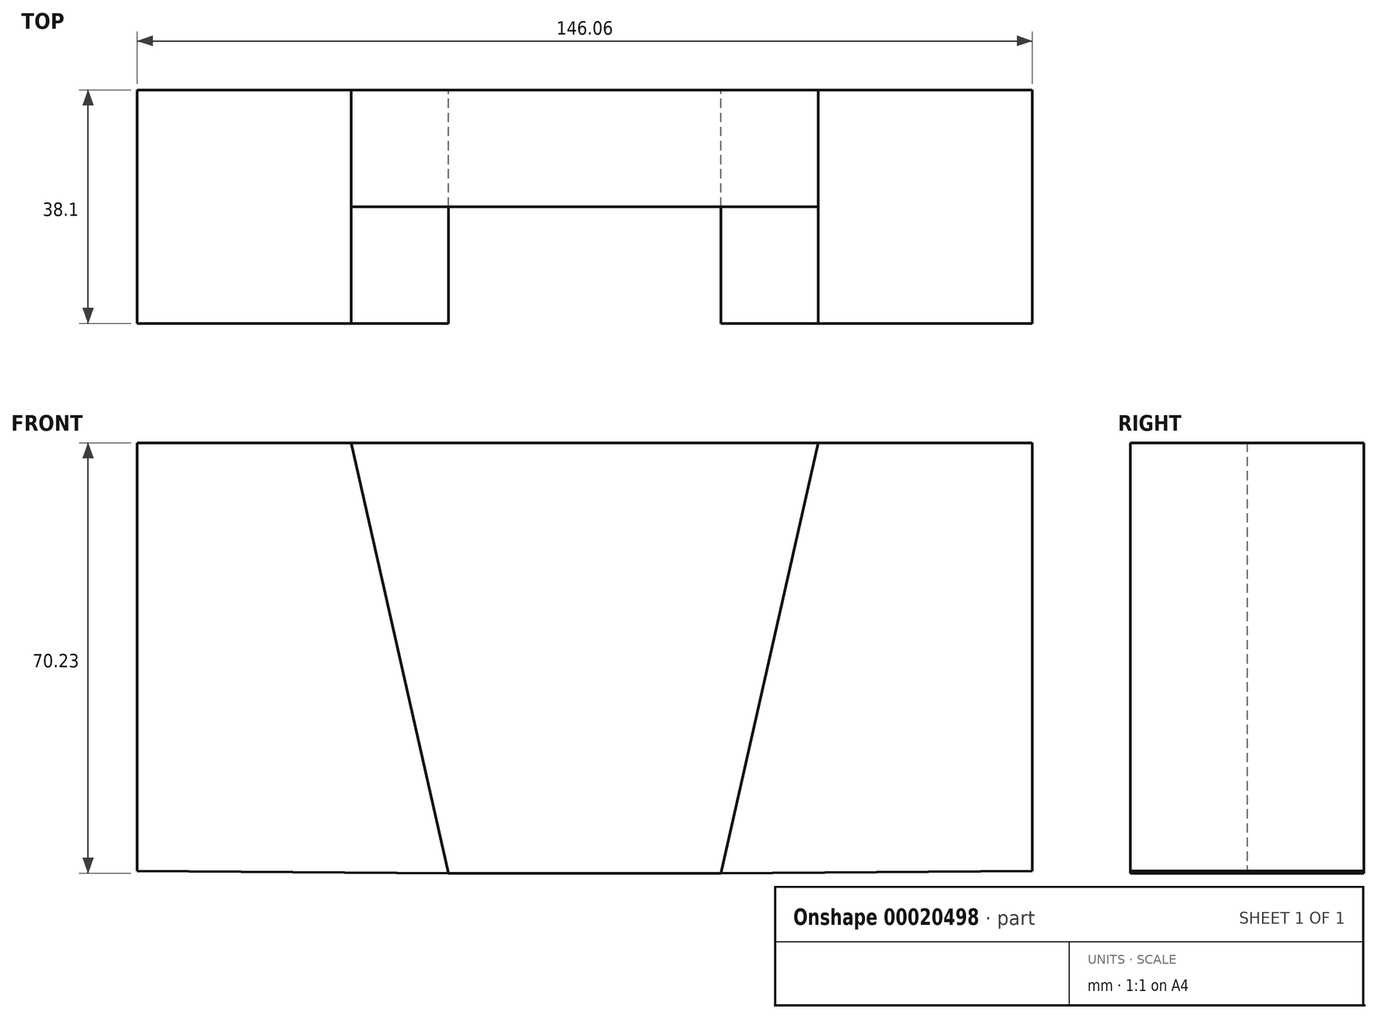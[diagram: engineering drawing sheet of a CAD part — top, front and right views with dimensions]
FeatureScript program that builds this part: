
annotation { "Feature Type Name" : "Feature", "Feature Type Description" : "" }
export const myFeature = defineFeature(function(context is Context, id is Id, definition is map)
    precondition{}
    {
        {
            var Q0;
            Q0=qCreatedBy(makeId("Front.planeOp"),FACE);
            var sketch = newSketch(context, id + "F0", { "sketchPlane" : qUnion([Q0])});
            skLineSegment(sketch, "E0", {"start": v(-73.02, 35.2) * mm, "end": v(-73.02, -34.64) * mm});
            skLineSegment(sketch, "E1", {"start": v(-38.1, 35.2) * mm, "end": v(-22.22, -35.02) * mm});
            skLineSegment(sketch, "E2", {"start": v(-73.02, -34.64) * mm, "end": v(-22.22, -35.02) * mm});
            skLineSegment(sketch, "E3", {"start": v(-38.1, 35.2) * mm, "end": v(0, 35.2) * mm});
            skLineSegment(sketch, "E4", {"start": v(0, 35.2) * mm, "end": v(0, -35.02) * mm});
            skLineSegment(sketch, "E5.MirrorCS", {"start": v(38.1, 35.2) * mm, "end": v(22.23, -35.02) * mm});
            skLineSegment(sketch, "E6.MirrorCS", {"start": v(38.1, 35.2) * mm, "end": v(0, 35.2) * mm});
            skLineSegment(sketch, "E7.MirrorCS", {"start": v(73.03, 35.2) * mm, "end": v(73.03, -34.64) * mm});
            skLineSegment(sketch, "E8.MirrorCS", {"start": v(73.02, -34.64) * mm, "end": v(22.23, -35.02) * mm});
            skLineSegment(sketch, "E9", {"start": v(-73.03, 35.2) * mm, "end": v(-38.1, 35.2) * mm});
            skLineSegment(sketch, "E10", {"start": v(38.1, 35.2) * mm, "end": v(73.03, 35.2) * mm});
            skLineSegment(sketch, "E11", {"start": v(-22.23, -35.02) * mm, "end": v(22.23, -35.02) * mm});
            skSolve(sketch);
        }
        {
            var Q0;
            Q0=makeQuery(id+"F0.imprint","IMPRINT",FACE,{"disambiguationData":[TD([[makeQuery(id+"F0.imprint","IMPRINT",EDGE,{"derivedFrom":sQuery(id+"F0.wireOp",EDGE,"E0")}),1.0]])]});
            var Q1;
            Q1=makeQuery(id+"F0.imprint","IMPRINT",FACE,{"disambiguationData":[TD([[makeQuery(id+"F0.imprint","IMPRINT",EDGE,{"derivedFrom":sQuery(id+"F0.wireOp",EDGE,"E5.MirrorCS")}),1.0]])]});
            extrude(context, id + "F1", {"entities" : qUnion([Q0, Q1]), "depth" : 38.1 * mm});
        }
        {
            var Q0;
            Q0=makeQuery(id+"F0.imprint","IMPRINT",FACE,{"disambiguationData":[TD([[makeQuery(id+"F0.imprint","IMPRINT",EDGE,{"derivedFrom":sQuery(id+"F0.wireOp",EDGE,"E1")}),1.0]])]});
            var Q1;
            Q1=makeQuery(id+"F0.imprint","IMPRINT",FACE,{"disambiguationData":[TD([[makeQuery(id+"F0.imprint","IMPRINT",EDGE,{"derivedFrom":sQuery(id+"F0.wireOp",EDGE,"E4")}),1.0]])]});
            extrude(context, id + "F2", {"entities" : qUnion([Q0, Q1]), "depth" : 19.05 * mm});
        }
    });
